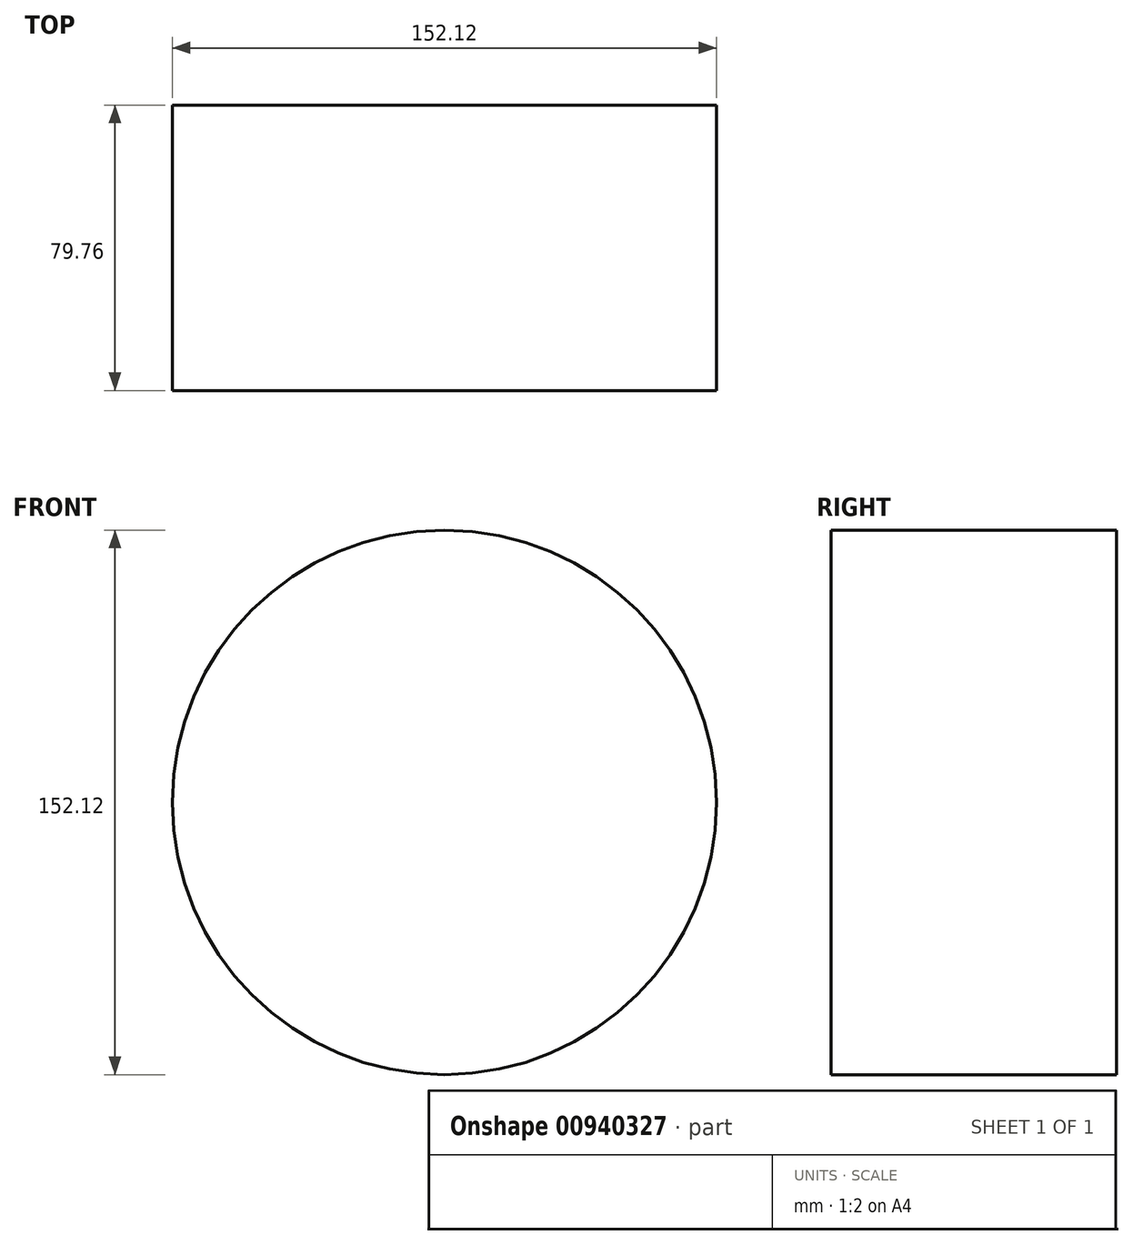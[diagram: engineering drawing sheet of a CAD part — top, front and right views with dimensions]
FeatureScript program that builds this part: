
annotation { "Feature Type Name" : "Feature", "Feature Type Description" : "" }
export const myFeature = defineFeature(function(context is Context, id is Id, definition is map)
    precondition{}
    {
        {
            var Q0;
            Q0=qCreatedBy(makeId("Front.planeOp"),FACE);
            var sketch = newSketch(context, id + "F0", { "sketchPlane" : qUnion([Q0])});
            skCircle(sketch, "E0", {"center": v(0, 0) * mm, "radius": 76.06 * mm});
            skSolve(sketch);
        }
        {
            var Q0;
            Q0=makeQuery(id+"F0.imprint","IMPRINT",FACE,{"disambiguationData":[TD([[makeQuery(id+"F0.imprint","IMPRINT",EDGE,{"derivedFrom":sQuery(id+"F0.wireOp",EDGE,"E0")}),1.0]])]});
            extrude(context, id + "F1", {"entities" : qUnion([Q0]), "depth" : 79.76 * mm, "offsetDistance" : 25.4 * mm});
        }
    });
